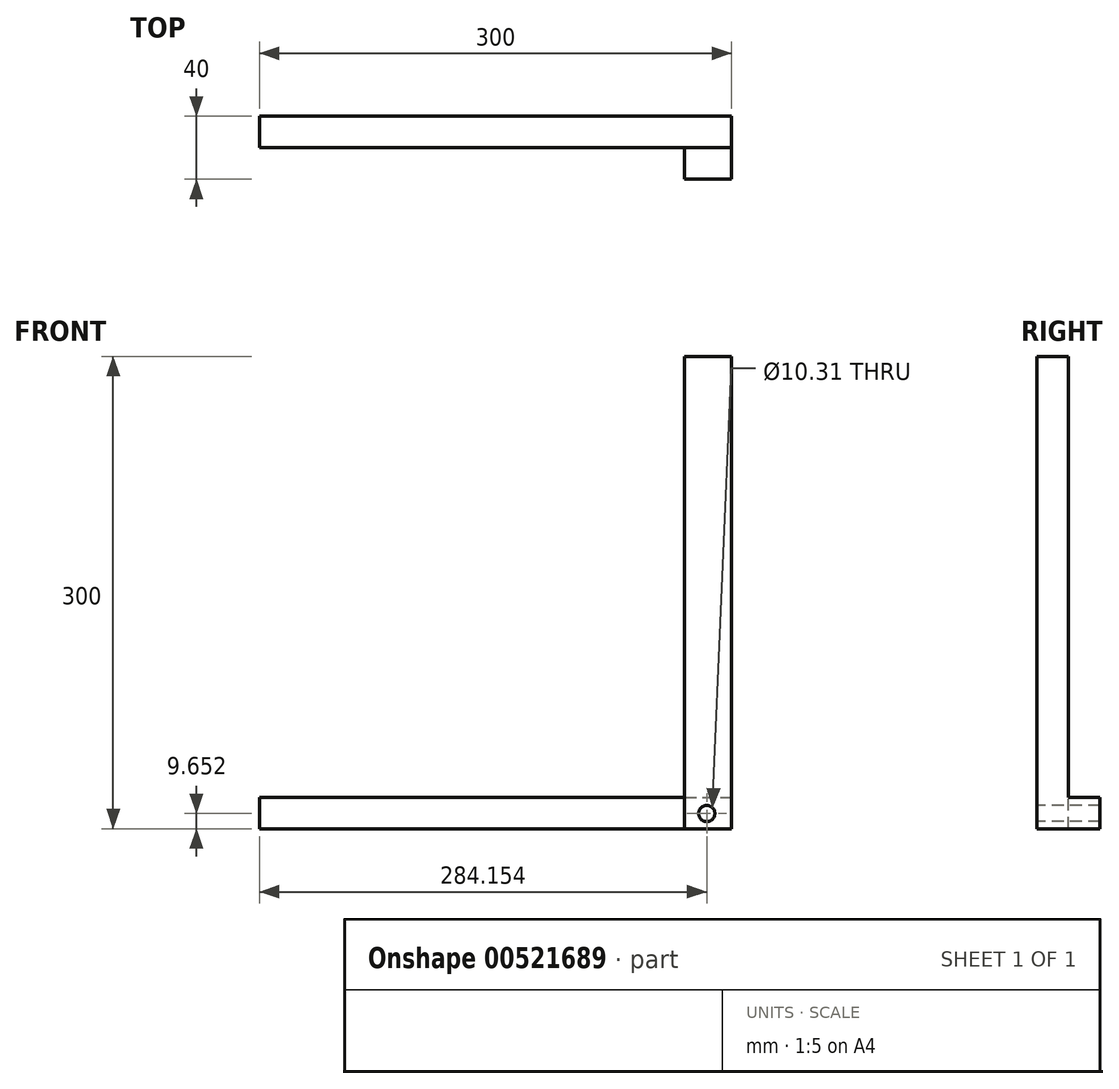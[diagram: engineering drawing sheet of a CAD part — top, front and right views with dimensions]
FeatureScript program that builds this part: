
annotation { "Feature Type Name" : "Feature", "Feature Type Description" : "" }
export const myFeature = defineFeature(function(context is Context, id is Id, definition is map)
    precondition{}
    {
        {
            var Q0;
            Q0=qCreatedBy(makeId("Front.planeOp"),FACE);
            var sketch = newSketch(context, id + "F0", { "sketchPlane" : qUnion([Q0])});
            skLineSegment(sketch, "E0.bottom", {"start": v(-56.17, 20) * mm, "end": v(243.83, 20) * mm});
            skLineSegment(sketch, "E0.top", {"start": v(-56.17, 0) * mm, "end": v(243.83, 0) * mm});
            skLineSegment(sketch, "E0.left", {"start": v(-56.17, 20) * mm, "end": v(-56.17, 0) * mm});
            skLineSegment(sketch, "E0.right", {"start": v(243.83, 20) * mm, "end": v(243.83, 0) * mm});
            skSolve(sketch);
        }
        {
            var Q0;
            Q0 = qSketchRegion(id + "F0", true);
            extrude(context, id + "F1", {"entities" : qUnion([Q0]), "depth" : 20 * mm, "offsetDistance" : 25 * mm});
        }
        {
            var Q0;
            Q0=makeQuery(id+"F1.opExtrude","CAP_FACE",FACE,{"disambiguationData":[OSD([sQuery(id+"F0.wireOp",EDGE,"E0.bottom"),sQuery(id+"F0.wireOp",EDGE,"E0.top"),sQuery(id+"F0.wireOp",EDGE,"E0.left"),sQuery(id+"F0.wireOp",EDGE,"E0.right")])],"isStart":false});
            var sketch = newSketch(context, id + "F2", { "sketchPlane" : qUnion([Q0])});
            skCircle(sketch, "E1", {"center": v(227.98, 9.65) * mm, "radius": 5.15 * mm});
            skSolve(sketch);
        }
        {
            var Q0;
            Q0 = qSketchRegion(id + "F2", true);
            extrude(context, id + "F3", {"entities" : qUnion([Q0]), "operationType" : NewBodyOperationType.REMOVE, "endBound" : BoundingType.THROUGH_ALL, "oppositeDirection" : true, "depth" : 25 * mm, "offsetDistance" : 25 * mm});
        }
        {
            var Q0;
            Q0=makeQuery(id+"F1.opExtrude","CAP_FACE",FACE,{"disambiguationData":[OSD([sQuery(id+"F0.wireOp",EDGE,"E0.bottom"),sQuery(id+"F0.wireOp",EDGE,"E0.top"),sQuery(id+"F0.wireOp",EDGE,"E0.left"),sQuery(id+"F0.wireOp",EDGE,"E0.right")])],"isStart":false});
            var sketch = newSketch(context, id + "F4", { "sketchPlane" : qUnion([Q0])});
            skLineSegment(sketch, "E2.bottom", {"start": v(243.83, 0) * mm, "end": v(213.83, 0) * mm});
            skLineSegment(sketch, "E2.top", {"start": v(243.83, 300) * mm, "end": v(213.83, 300) * mm});
            skLineSegment(sketch, "E2.left", {"start": v(243.83, 0) * mm, "end": v(243.83, 300) * mm});
            skLineSegment(sketch, "E2.right", {"start": v(213.83, 0) * mm, "end": v(213.83, 300) * mm});
            skSolve(sketch);
        }
        {
            var Q0;
            Q0 = qSketchRegion(id + "F4", true);
            extrude(context, id + "F5", {"entities" : qUnion([Q0]), "operationType" : NewBodyOperationType.ADD, "depth" : 20 * mm, "offsetDistance" : 25 * mm});
        }
        {
            var Q0;
            Q0=makeQuery(id+"F5.opExtrude","CAP_FACE",FACE,{"disambiguationData":[OSD([sQuery(id+"F4.wireOp",EDGE,"E2.bottom"),sQuery(id+"F4.wireOp",EDGE,"E2.top"),sQuery(id+"F4.wireOp",EDGE,"E2.left"),sQuery(id+"F4.wireOp",EDGE,"E2.right")])],"isStart":false});
            var sketch = newSketch(context, id + "F6", { "sketchPlane" : qUnion([Q0])});
            skCircle(sketch, "E3", {"center": v(227.98, 9.65) * mm, "radius": 5.15 * mm});
            skSolve(sketch);
        }
        {
            var Q0;
            Q0 = qSketchRegion(id + "F6", true);
            extrude(context, id + "F7", {"entities" : qUnion([Q0]), "operationType" : NewBodyOperationType.REMOVE, "oppositeDirection" : true, "depth" : 25 * mm, "offsetDistance" : 25 * mm});
        }
    });
